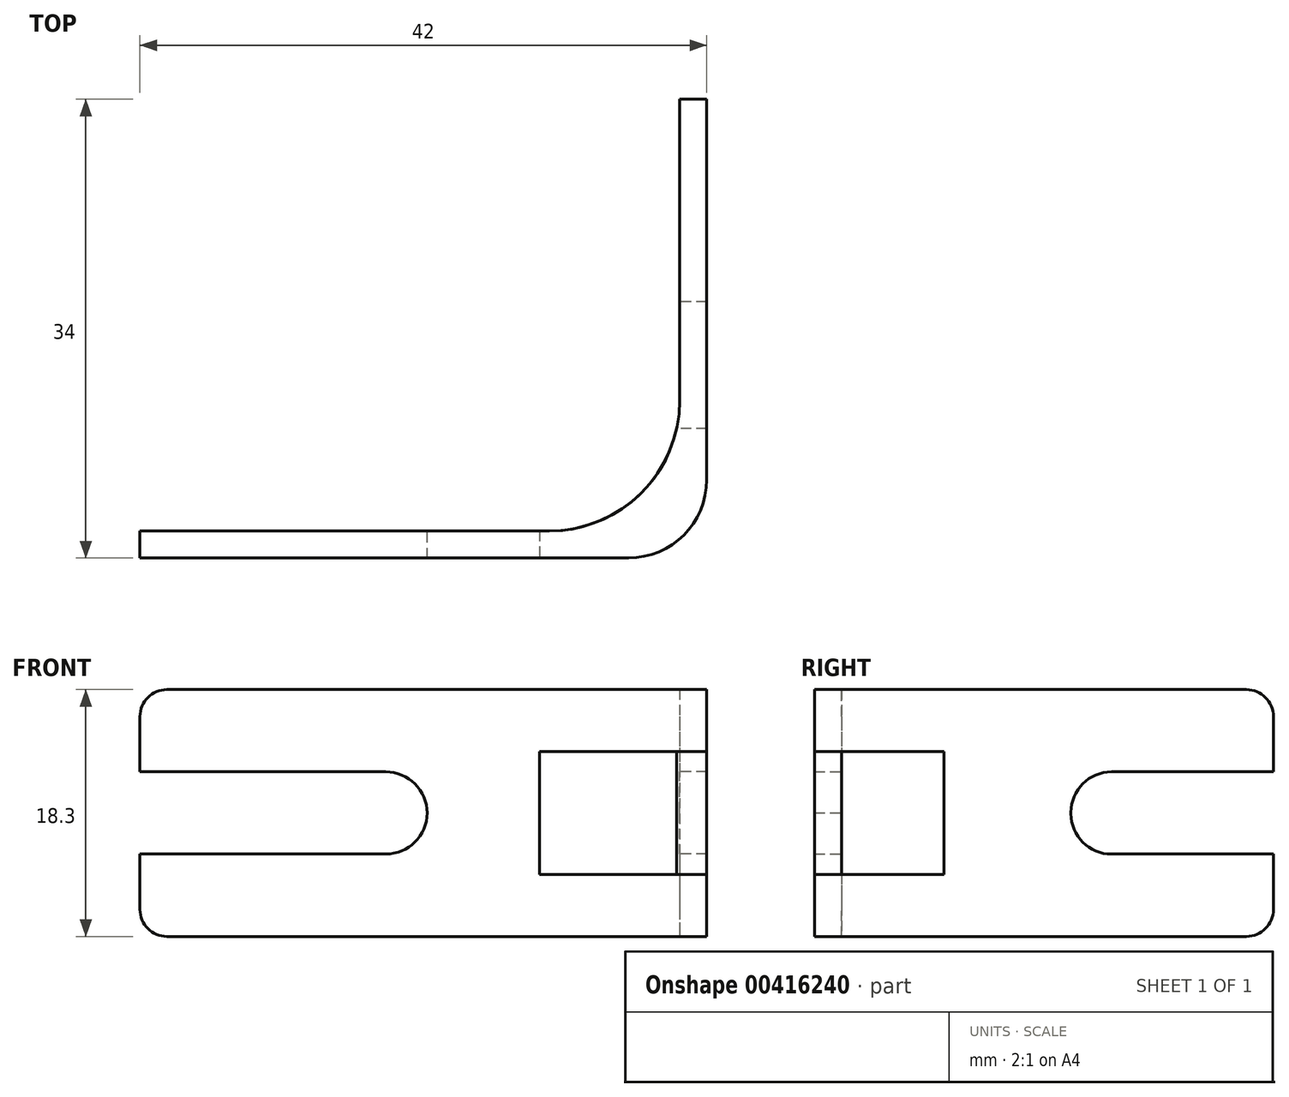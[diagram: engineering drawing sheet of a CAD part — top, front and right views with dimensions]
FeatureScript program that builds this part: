
annotation { "Feature Type Name" : "Feature", "Feature Type Description" : "" }
export const myFeature = defineFeature(function(context is Context, id is Id, definition is map)
    precondition{}
    {
        {
            var Q0;
            Q0=qCreatedBy(makeId("Top.planeOp"),FACE);
            var sketch = newSketch(context, id + "F0", { "sketchPlane" : qUnion([Q0])});
            skLineSegment(sketch, "E0", {"start": v(-35.77, -18.89) * mm, "end": v(4.23, -18.89) * mm});
            skLineSegment(sketch, "E1", {"start": v(4.23, -18.89) * mm, "end": v(4.23, 13.11) * mm});
            skLineSegment(sketch, "E2", {"start": v(4.23, 13.11) * mm, "end": v(6.23, 13.11) * mm});
            skLineSegment(sketch, "E3", {"start": v(6.23, 13.11) * mm, "end": v(6.23, -20.89) * mm});
            skLineSegment(sketch, "E4", {"start": v(6.23, -20.89) * mm, "end": v(-35.77, -20.89) * mm});
            skLineSegment(sketch, "E5", {"start": v(-35.77, -20.89) * mm, "end": v(-35.77, -18.89) * mm});
            skSolve(sketch);
        }
        {
            var Q0;
            Q0 = qSketchRegion(id + "F0", true);
            extrude(context, id + "F1", {"entities" : qUnion([Q0]), "depth" : 18.3 * mm});
        }
        {
            var Q0;
            Q0=makeQuery(id+"F1.opExtrude","SWEPT_FACE",FACE,{"disambiguationData":[OSD([sQuery(id+"F0.wireOp",EDGE,"E0")])]});
            var sketch = newSketch(context, id + "F2", { "sketchPlane" : qUnion([Q0])});
            skLineSegment(sketch, "E6", {"start": v(35.77, 6.1) * mm, "end": v(18.47, 6.1) * mm});
            skLineSegment(sketch, "E7", {"start": v(18.47, 6.1) * mm, "end": v(18.47, 12.2) * mm});
            skLineSegment(sketch, "E8", {"start": v(18.47, 12.2) * mm, "end": v(35.77, 12.2) * mm});
            skLineSegment(sketch, "E9", {"start": v(35.77, 0) * mm, "end": v(35.77, 18.3) * mm});
            skSolve(sketch);
        }
        {
            var Q0;
            Q0 = qSketchRegion(id + "F2", true);
            extrude(context, id + "F3", {"entities" : qUnion([Q0]), "operationType" : NewBodyOperationType.REMOVE, "oppositeDirection" : true, "depth" : 25 * mm});
        }
        {
            var Q0;
            Q0=makeQuery(id+"F1.opExtrude","SWEPT_EDGE",EDGE,{"disambiguationData":[OSD([sQuery(id+"F0.wireOp",EDGE,"E0"),sQuery(id+"F0.wireOp",EDGE,"E1")])]});
            fillet(context, id + "F4", {"entities" : qUnion([Q0]), "radius" : 9.66 * mm, "tangentPropagation" : true, "allowEdgeOverflow" : false});
        }
        {
            var Q0;
            Q0=makeQuery(id+"F1.opExtrude","SWEPT_EDGE",EDGE,{"disambiguationData":[OSD([sQuery(id+"F0.wireOp",EDGE,"E3"),sQuery(id+"F0.wireOp",EDGE,"E4")])]});
            fillet(context, id + "F5", {"entities" : qUnion([Q0]), "radius" : 5.8 * mm, "tangentPropagation" : true, "allowEdgeOverflow" : false});
        }
        {
            var Q0;
            Q0=makeQuery(id+"F1.opExtrude","SWEPT_FACE",FACE,{"disambiguationData":[OSD([sQuery(id+"F0.wireOp",EDGE,"E1")])]});
            var sketch = newSketch(context, id + "F6", { "sketchPlane" : qUnion([Q0])});
            skLineSegment(sketch, "E10", {"start": v(-13.11, 6.1) * mm, "end": v(1.89, 6.1) * mm});
            skLineSegment(sketch, "E11", {"start": v(1.89, 6.1) * mm, "end": v(1.89, 12.2) * mm});
            skLineSegment(sketch, "E12", {"start": v(1.89, 12.2) * mm, "end": v(-13.11, 12.2) * mm});
            skLineSegment(sketch, "E13", {"start": v(-13.11, 12.2) * mm, "end": v(-13.11, 6.1) * mm});
            skSolve(sketch);
        }
        {
            var Q0;
            Q0 = qSketchRegion(id + "F6", true);
            extrude(context, id + "F7", {"entities" : qUnion([Q0]), "operationType" : NewBodyOperationType.REMOVE, "oppositeDirection" : true, "depth" : 25 * mm});
        }
        {
            var Q0;
            Q0=makeQuery(id+"F7.boolean.opBoolean","COPY",EDGE,{"derivedFrom":makeQuery(id+"F7.opExtrude","SWEPT_EDGE",EDGE,{"disambiguationData":[OSD([sQuery(id+"F6.wireOp",EDGE,"E10"),sQuery(id+"F6.wireOp",EDGE,"E11")])]})});
            var Q1;
            Q1=makeQuery(id+"F7.boolean.opBoolean","COPY",EDGE,{"derivedFrom":makeQuery(id+"F7.opExtrude","SWEPT_EDGE",EDGE,{"disambiguationData":[OSD([sQuery(id+"F6.wireOp",EDGE,"E11"),sQuery(id+"F6.wireOp",EDGE,"E12")])]})});
            fillet(context, id + "F8", {"entities" : qUnion([Q0, Q1]), "radius" : 3 * mm, "tangentPropagation" : true, "allowEdgeOverflow" : false});
        }
        {
            var Q0;
            Q0=makeQuery(id+"F1.opExtrude","CAP_EDGE",EDGE,{"disambiguationData":[OSD([sQuery(id+"F0.wireOp",EDGE,"E2")])],"isStart":true});
            var Q1;
            Q1=makeQuery(id+"F1.opExtrude","CAP_EDGE",EDGE,{"disambiguationData":[OSD([sQuery(id+"F0.wireOp",EDGE,"E2")])],"isStart":false});
            var Q2;
            Q2=makeQuery(id+"F1.opExtrude","CAP_EDGE",EDGE,{"disambiguationData":[OSD([sQuery(id+"F0.wireOp",EDGE,"E5")])],"isStart":true});
            var Q3;
            Q3=makeQuery(id+"F1.opExtrude","CAP_EDGE",EDGE,{"disambiguationData":[OSD([sQuery(id+"F0.wireOp",EDGE,"E5")])],"isStart":false});
            fillet(context, id + "F9", {"entities" : qUnion([Q0, Q1, Q2, Q3]), "radius" : 2 * mm, "tangentPropagation" : true, "allowEdgeOverflow" : false});
        }
        {
            var Q0;
            Q0=makeQuery(id+"F1.opExtrude","SWEPT_FACE",FACE,{"disambiguationData":[OSD([sQuery(id+"F0.wireOp",EDGE,"E4")])]});
            var sketch = newSketch(context, id + "F10", { "sketchPlane" : qUnion([Q0])});
            skLineSegment(sketch, "E14", {"start": v(7.6, 9.2) * mm, "end": v(7.6, 6.1) * mm});
            skLineSegment(sketch, "E15", {"start": v(7.6, 6.1) * mm, "end": v(-4.16, 6.1) * mm});
            skLineSegment(sketch, "E16", {"start": v(-4.16, 6.1) * mm, "end": v(-4.16, 12.2) * mm});
            skLineSegment(sketch, "E17", {"start": v(-4.16, 12.2) * mm, "end": v(7.6, 12.2) * mm});
            skLineSegment(sketch, "E18", {"start": v(7.6, 12.2) * mm, "end": v(7.6, 9.2) * mm});
            skSolve(sketch);
        }
        {
            var Q0;
            Q0 = qSketchRegion(id + "F10", true);
            extrude(context, id + "F11", {"entities" : qUnion([Q0]), "operationType" : NewBodyOperationType.REMOVE, "oppositeDirection" : true, "depth" : 7.6 * mm});
        }
        {
            var Q0;
            Q0=makeQuery(id+"F1.opExtrude","SWEPT_FACE",FACE,{"disambiguationData":[OSD([sQuery(id+"F0.wireOp",EDGE,"E0")])]});
            var sketch = newSketch(context, id + "F12", { "sketchPlane" : qUnion([Q0])});
            skLineSegment(sketch, "E19", {"start": v(18.47, 12.2) * mm, "end": v(14.48, 12.2) * mm});
            skLineSegment(sketch, "E20", {"start": v(14.48, 12.2) * mm, "end": v(14.48, 6.1) * mm});
            skLineSegment(sketch, "E21", {"start": v(14.48, 6.1) * mm, "end": v(18.47, 6.1) * mm});
            skLineSegment(sketch, "E22", {"start": v(18.47, 6.1) * mm, "end": v(18.47, 12.2) * mm});
            skSolve(sketch);
        }
        {
            var Q0;
            Q0 = qSketchRegion(id + "F12", true);
            extrude(context, id + "F13", {"entities" : qUnion([Q0]), "operationType" : NewBodyOperationType.REMOVE, "oppositeDirection" : true, "depth" : 25 * mm});
        }
        {
            var Q0;
            Q0=makeQuery(id+"F13.boolean.opBoolean","COPY",EDGE,{"derivedFrom":makeQuery(id+"F13.opExtrude","SWEPT_EDGE",EDGE,{"disambiguationData":[OSD([sQuery(id+"F12.wireOp",EDGE,"E20"),sQuery(id+"F12.wireOp",EDGE,"E21")])]})});
            var Q1;
            Q1=makeQuery(id+"F13.boolean.opBoolean","COPY",EDGE,{"derivedFrom":makeQuery(id+"F13.opExtrude","SWEPT_EDGE",EDGE,{"disambiguationData":[OSD([sQuery(id+"F12.wireOp",EDGE,"E19"),sQuery(id+"F12.wireOp",EDGE,"E20")])]})});
            fillet(context, id + "F14", {"entities" : qUnion([Q0, Q1]), "radius" : 3.07 * mm, "tangentPropagation" : true, "allowEdgeOverflow" : false});
        }
        {
            var Q0;
            Q0=makeQuery(id+"F11.boolean.opBoolean","COPY",FACE,{"derivedFrom":makeQuery(id+"F11.opExtrude","SWEPT_FACE",FACE,{"disambiguationData":[OSD([sQuery(id+"F10.wireOp",EDGE,"E15")])]})});
            var Q1;
            Q1=makeQuery(id+"F11.boolean.opBoolean","COPY",FACE,{"derivedFrom":makeQuery(id+"F11.opExtrude","SWEPT_FACE",FACE,{"disambiguationData":[OSD([sQuery(id+"F10.wireOp",EDGE,"E17")])]})});
            extrude(context, id + "F15", {"entities" : qUnion([Q0, Q1]), "operationType" : NewBodyOperationType.REMOVE, "oppositeDirection" : true, "depth" : 1 * mm, "offsetDistance" : 25 * mm});
        }
        {
            var Q0;
            Q0=makeQuery(id+"F11.boolean.opBoolean","COPY",FACE,{"derivedFrom":makeQuery(id+"F11.opExtrude","SWEPT_FACE",FACE,{"disambiguationData":[OSD([sQuery(id+"F10.wireOp",EDGE,"E17")])]})});
            extrude(context, id + "F16", {"entities" : qUnion([Q0]), "operationType" : NewBodyOperationType.REMOVE, "oppositeDirection" : true, "depth" : 1 * mm, "offsetDistance" : 25 * mm});
        }
        {
            var Q0;
            {var subQ0=sQuery(id+"F10.wireOp",EDGE,"E16");Q0=makeQuery(id+"F16.boolean.opBoolean","MERGE",FACE,{"derivedFrom":[makeQuery(id+"F15.boolean.opBoolean","MERGE",FACE,{"derivedFrom":[makeQuery(id+"F11.boolean.opBoolean","COPY",FACE,{"derivedFrom":makeQuery(id+"F11.opExtrude","SWEPT_FACE",FACE,{"disambiguationData":[OSD([subQ0])]})}),makeQuery(id+"F15.opExtrude","SWEPT_FACE",FACE,{"disambiguationData":[OSD([sQuery(id+"F10.wireOp",EDGE,"E15"),subQ0])]})]}),makeQuery(id+"F16.opExtrude","SWEPT_FACE",FACE,{"disambiguationData":[OSD([subQ0,sQuery(id+"F10.wireOp",EDGE,"E17")])]})]});}
            extrude(context, id + "F17", {"entities" : qUnion([Q0]), "operationType" : NewBodyOperationType.REMOVE, "oppositeDirection" : true, "depth" : 2 * mm, "offsetDistance" : 25 * mm});
        }
        {
            var Q0;
            {var subQ0=sQuery(id+"F10.wireOp",EDGE,"E17");var subQ1=sQuery(id+"F10.wireOp",EDGE,"E15");Q0=makeQuery(id+"F16.boolean.opBoolean","MERGE",FACE,{"derivedFrom":[makeQuery(id+"F15.boolean.opBoolean","MERGE",FACE,{"derivedFrom":[makeQuery(id+"F11.boolean.opBoolean","COPY",FACE,{"derivedFrom":makeQuery(id+"F11.opExtrude","CAP_FACE",FACE,{"disambiguationData":[OSD([sQuery(id+"F10.wireOp",EDGE,"E14"),subQ1,sQuery(id+"F10.wireOp",EDGE,"E16"),subQ0,sQuery(id+"F10.wireOp",EDGE,"E18")])],"isStart":false})}),makeQuery(id+"F15.opExtrude","SWEPT_FACE",FACE,{"disambiguationData":[OSD([subQ1]),TDD([makeQuery(id+"F11.boolean.opBoolean","COPY",EDGE,{"derivedFrom":makeQuery(id+"F11.opExtrude","CAP_EDGE",EDGE,{"disambiguationData":[OSD([subQ1])],"isStart":false})})])]})]}),makeQuery(id+"F16.opExtrude","SWEPT_FACE",FACE,{"disambiguationData":[OSD([subQ0]),TDD([makeQuery(id+"F11.boolean.opBoolean","COPY",EDGE,{"derivedFrom":makeQuery(id+"F11.opExtrude","CAP_EDGE",EDGE,{"disambiguationData":[OSD([subQ0])],"isStart":false})})])]})]});}
            extrude(context, id + "F18", {"entities" : qUnion([Q0]), "operationType" : NewBodyOperationType.REMOVE, "oppositeDirection" : true, "depth" : 2 * mm, "offsetDistance" : 25 * mm});
        }
        {
            var Q0;
            {var subQ0=sQuery(id+"F10.wireOp",EDGE,"E17");Q0=makeQuery(id+"F18.boolean.opBoolean","MERGE",FACE,{"derivedFrom":[makeQuery(id+"F17.boolean.opBoolean","MERGE",FACE,{"derivedFrom":[makeQuery(id+"F16.boolean.opBoolean","COPY",FACE,{"derivedFrom":makeQuery(id+"F16.opExtrude","CAP_FACE",FACE,{"disambiguationData":[OSD([subQ0])],"isStart":false})}),makeQuery(id+"F17.opExtrude","SWEPT_FACE",FACE,{"disambiguationData":[OSD([sQuery(id+"F10.wireOp",EDGE,"E16"),subQ0])]})]}),makeQuery(id+"F18.opExtrude","SWEPT_FACE",FACE,{"disambiguationData":[OSD([subQ0])]})]});}
            extrude(context, id + "F19", {"entities" : qUnion([Q0]), "operationType" : NewBodyOperationType.REMOVE, "oppositeDirection" : true, "depth" : 0.5 * mm, "offsetDistance" : 25 * mm});
        }
        {
            var Q0;
            {var subQ0=sQuery(id+"F10.wireOp",EDGE,"E15");Q0=makeQuery(id+"F18.boolean.opBoolean","MERGE",FACE,{"derivedFrom":[makeQuery(id+"F17.boolean.opBoolean","MERGE",FACE,{"derivedFrom":[makeQuery(id+"F15.boolean.opBoolean","COPY",FACE,{"derivedFrom":makeQuery(id+"F15.opExtrude","CAP_FACE",FACE,{"disambiguationData":[OSD([subQ0])],"isStart":false})}),makeQuery(id+"F17.opExtrude","SWEPT_FACE",FACE,{"disambiguationData":[OSD([subQ0,sQuery(id+"F10.wireOp",EDGE,"E16")])]})]}),makeQuery(id+"F18.opExtrude","SWEPT_FACE",FACE,{"disambiguationData":[OSD([subQ0])]})]});}
            extrude(context, id + "F20", {"entities" : qUnion([Q0]), "operationType" : NewBodyOperationType.REMOVE, "oppositeDirection" : true, "depth" : 0.5 * mm, "offsetDistance" : 25 * mm});
        }
    });
